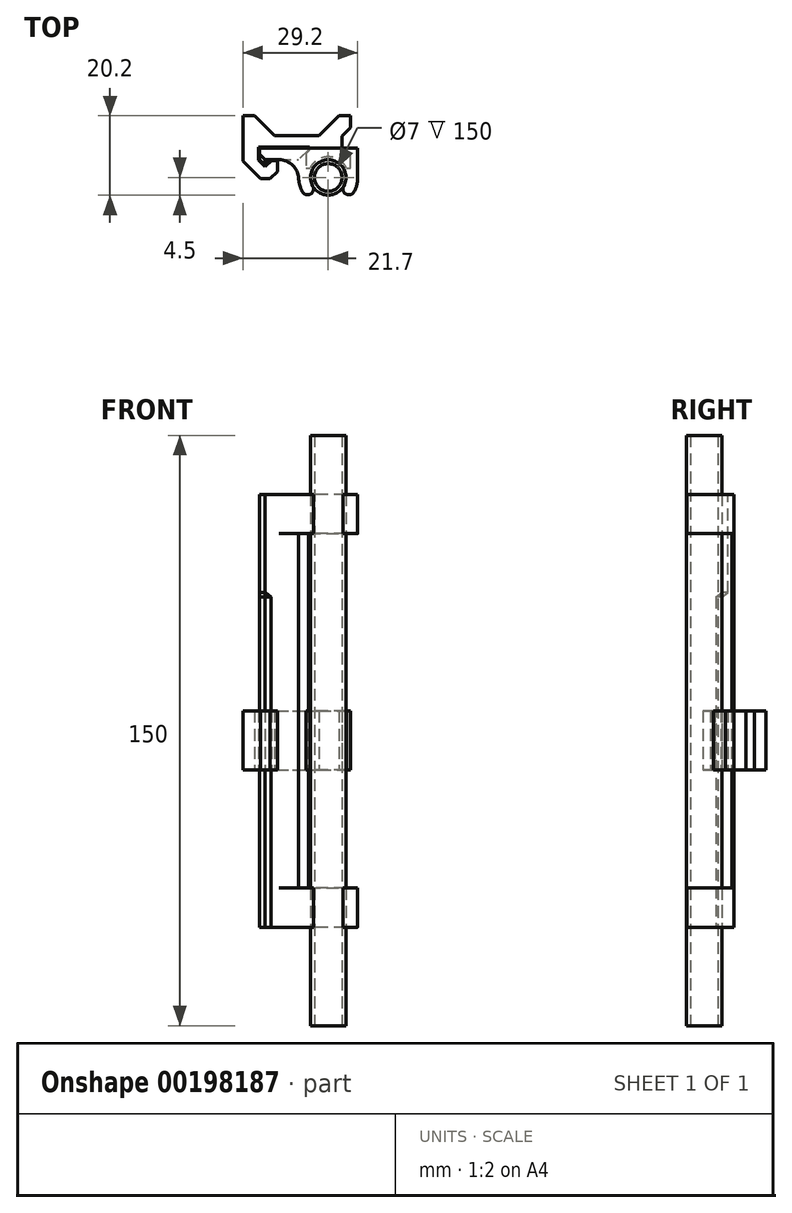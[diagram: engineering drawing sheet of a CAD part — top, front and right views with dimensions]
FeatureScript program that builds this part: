
annotation { "Feature Type Name" : "Feature", "Feature Type Description" : "" }
export const myFeature = defineFeature(function(context is Context, id is Id, definition is map)
    precondition{}
    {
        {
            var Q0;
            Q0=qCreatedBy(makeId("Top.planeOp"),FACE);
            var sketch = newSketch(context, id + "F0", { "sketchPlane" : qUnion([Q0])});
            skArc(sketch, "E0", {"start": v(-6.56, -3.63) * mm, "mid": v(-4.52, -4.22) * mm, "end": v(-3.94, -2.18) * mm});
            skArc(sketch, "E1.MirrorCS", {"start": v(6.56, -3.63) * mm, "mid": v(4.52, -4.22) * mm, "end": v(3.94, -2.18) * mm});
            skArc(sketch, "E2", {"start": v(-3.94, -2.18) * mm, "mid": v(0, -4.5) * mm, "end": v(3.94, -2.18) * mm, "construction": true});
            skArc(sketch, "E3", {"start": v(3.94, -2.18) * mm, "mid": v(0, 4.5) * mm, "end": v(-3.94, -2.18) * mm});
            skArc(sketch, "E4", {"start": v(6.56, -3.63) * mm, "mid": v(7.26, -1.87) * mm, "end": v(7.5, 0) * mm});
            skArc(sketch, "E5", {"start": v(-6.56, -3.63) * mm, "mid": v(0, -7.5) * mm, "end": v(6.56, -3.63) * mm, "construction": true});
            skLineSegment(sketch, "E6.right", {"start": v(-17.5, 4.5) * mm, "end": v(-17.5, 7.5) * mm});
            skArc(sketch, "E7", {"start": v(-7.5, 0) * mm, "mid": v(-7.26, -1.87) * mm, "end": v(-6.56, -3.63) * mm});
            skLineSegment(sketch, "E8", {"start": v(-7.5, 4.5) * mm, "end": v(-17.5, 4.5) * mm});
            skArc(sketch, "E9", {"start": v(7.5, 0) * mm, "mid": v(0, 7.5) * mm, "end": v(-7.5, 0) * mm, "construction": true});
            skLineSegment(sketch, "E10", {"start": v(7.5, 0) * mm, "end": v(7.5, 7.5) * mm});
            skPoint(sketch, "E10.endSnap0", {"position": v(0, 7.5) * mm});
            skLineSegment(sketch, "E11", {"start": v(-17.5, 7.5) * mm, "end": v(7.5, 7.5) * mm});
            skLineSegment(sketch, "E12", {"start": v(-7.5, 0) * mm, "end": v(-7.5, 4.5) * mm});
            skLineSegment(sketch, "E13", {"start": v(-4.5, 0) * mm, "end": v(-4.5, 7.5) * mm, "construction": true});
            skLineSegment(sketch, "E14", {"start": v(-7.5, 4.5) * mm, "end": v(-5, 7) * mm});
            skLineSegment(sketch, "E15", {"start": v(-5, 7) * mm, "end": v(-5, 7.5) * mm});
            skLineSegment(sketch, "E16", {"start": v(-5, 7) * mm, "end": v(-4.5, 7.5) * mm, "construction": true});
            skLineSegment(sketch, "E17", {"start": v(-17.5, 4.5) * mm, "end": v(-16, 3) * mm});
            skLineSegment(sketch, "E18", {"start": v(-16, 3) * mm, "end": v(-14.5, 4.5) * mm});
            skSolve(sketch);
        }
        {
            var Q0;
            Q0=qCreatedBy(makeId("Top.planeOp"),FACE);
            var sketch = newSketch(context, id + "F1", { "sketchPlane" : qUnion([Q0])});
            skCircle(sketch, "E19", {"center": v(0, 0) * mm, "radius": 4.5 * mm});
            skCircle(sketch, "E20", {"center": v(0, 0) * mm, "radius": 3.5 * mm});
            skSolve(sketch);
        }
        {
            var Q0;
            Q0=qCreatedBy(makeId("Top.planeOp"),FACE);
            var sketch = newSketch(context, id + "F2", { "sketchPlane" : qUnion([Q0])});
            skLineSegment(sketch, "E21.0", {"start": v(-17.5, 4.5) * mm, "end": v(-17.5, 7.5) * mm, "construction": true});
            skLineSegment(sketch, "E22.0", {"start": v(-17.5, 4.5) * mm, "end": v(-16, 3) * mm, "construction": true});
            skLineSegment(sketch, "E23.0", {"start": v(-16, 3) * mm, "end": v(-14.5, 4.5) * mm, "construction": true});
            skLineSegment(sketch, "E24.0", {"start": v(-7.5, 4.5) * mm, "end": v(-14.5, 4.5) * mm, "construction": true});
            skLineSegment(sketch, "E25.0", {"start": v(-7.5, 4.5) * mm, "end": v(-5, 7) * mm, "construction": true});
            skLineSegment(sketch, "E26.0", {"start": v(-5, 7) * mm, "end": v(-5, 7.5) * mm, "construction": true});
            skLineSegment(sketch, "E27.0", {"start": v(-17.5, 7.5) * mm, "end": v(-5, 7.5) * mm, "construction": true});
            skPoint(sketch, "E28.orphan", {"position": v(-17.5, 4.5) * mm});
            skLineSegment(sketch, "E29.0", {"start": v(-17.7, 4.42) * mm, "end": v(-17.7, 7.7) * mm});
            skLineSegment(sketch, "E29.1", {"start": v(-17.7, 4.42) * mm, "end": v(-16, 2.72) * mm});
            skLineSegment(sketch, "E29.2", {"start": v(-4.8, 6.92) * mm, "end": v(-4.8, 7.7) * mm});
            skLineSegment(sketch, "E29.3", {"start": v(-5.68, 6.04) * mm, "end": v(-4.8, 6.92) * mm});
            skLineSegment(sketch, "E29.4", {"start": v(-7.42, 4.3) * mm, "end": v(-7.5, 4.3) * mm});
            skLineSegment(sketch, "E29.5", {"start": v(-17.7, 7.7) * mm, "end": v(-4.8, 7.7) * mm});
            skLineSegment(sketch, "E29.6", {"start": v(-16, 2.72) * mm, "end": v(-14.42, 4.3) * mm});
            skLineSegment(sketch, "E30.0", {"start": v(-7.5, 0) * mm, "end": v(-7.5, 4.5) * mm, "construction": true});
            skArc(sketch, "E31", {"start": v(-7.5, -0.5) * mm, "mid": v(-8.96, 3.04) * mm, "end": v(-12.5, 4.5) * mm, "construction": true});
            skLineSegment(sketch, "E32", {"start": v(-12.92, 4.3) * mm, "end": v(-12.92, 1.56) * mm});
            skLineSegment(sketch, "E33", {"start": v(-12.92, 1.56) * mm, "end": v(-14.76, -0.28) * mm});
            skLineSegment(sketch, "E34", {"start": v(-17.24, -0.28) * mm, "end": v(-21.7, 4.17) * mm});
            skLineSegment(sketch, "E35", {"start": v(-21.7, 4.17) * mm, "end": v(-21.7, 15.7) * mm});
            skLineSegment(sketch, "E36", {"start": v(-21.7, 15.7) * mm, "end": v(-18.7, 15.7) * mm});
            skLineSegment(sketch, "E37", {"start": v(-17.24, -0.28) * mm, "end": v(-14.76, -0.28) * mm});
            skPoint(sketch, "E38.orphan", {"position": v(-16, -1.53) * mm});
            skCircle(sketch, "E39.0", {"center": v(0, 0) * mm, "radius": 4.5 * mm, "construction": true});
            skLineSegment(sketch, "E40", {"start": v(-5.68, 6.04) * mm, "end": v(-5.68, 2.38) * mm});
            skArc(sketch, "E41", {"start": v(4.68, 2.38) * mm, "mid": v(0, 5.25) * mm, "end": v(-4.68, 2.38) * mm});
            skLineSegment(sketch, "E42", {"start": v(-5.68, 2.38) * mm, "end": v(-4.68, 2.38) * mm});
            skLineSegment(sketch, "E43", {"start": v(4.68, 2.38) * mm, "end": v(5.68, 2.38) * mm});
            skLineSegment(sketch, "E44", {"start": v(5.68, 2.38) * mm, "end": v(5.68, 5.38) * mm});
            skLineSegment(sketch, "E45.trimOffspring", {"start": v(-12.92, 4.3) * mm, "end": v(-14.42, 4.3) * mm});
            skLineSegment(sketch, "E46", {"start": v(-18.7, 15.7) * mm, "end": v(-13.7, 10.7) * mm});
            skLineSegment(sketch, "E47", {"start": v(-13.7, 10.7) * mm, "end": v(-2.32, 10.7) * mm});
            skLineSegment(sketch, "E48", {"start": v(-2.32, 10.7) * mm, "end": v(2.68, 15.7) * mm});
            skLineSegment(sketch, "E49.trimOffspring", {"start": v(2.68, 15.7) * mm, "end": v(5.68, 15.7) * mm});
            skLineSegment(sketch, "E50", {"start": v(5.68, 12.7) * mm, "end": v(3.52, 10.54) * mm});
            skLineSegment(sketch, "E51", {"start": v(3.52, 10.54) * mm, "end": v(3.52, 7.54) * mm});
            skLineSegment(sketch, "E52", {"start": v(3.52, 7.54) * mm, "end": v(5.68, 5.38) * mm});
            skLineSegment(sketch, "E53.trimOffspring", {"start": v(5.68, 12.7) * mm, "end": v(5.68, 15.7) * mm});
            skSolve(sketch);
        }
        {
            var Q0;
            {var subQ0=sQuery(id+"F0.wireOp",EDGE,"E6.right");Q0=makeQuery(id+"F0.imprint","IMPRINT",FACE,{"disambiguationData":[TD([[makeQuery(id+"F0.imprint","IMPRINT",EDGE,{"derivedFrom":subQ0}),-1.0]])]});}
            var Q1;
            Q1=makeQuery(id+"F0.imprint","IMPRINT",FACE,{"disambiguationData":[TD([[makeQuery(id+"F0.imprint","IMPRINT",EDGE,{"derivedFrom":sQuery(id+"F0.wireOp",EDGE,"E0")}),1.0]])]});
            var Q2;
            {var subQ0=sQuery(id+"F0.wireOp",EDGE,"E12");Q2=makeQuery(id+"F0.imprint","IMPRINT",FACE,{"disambiguationData":[TD([[makeQuery(id+"F0.imprint","IMPRINT",EDGE,{"derivedFrom":subQ0}),1.0]])]});}
            extrude(context, id + "F3", {"entities" : qUnion([Q0, Q1, Q2]), "depth" : 10 * mm});
        }
        {
            var Q0;
            Q0=makeQuery(id+"F3.opExtrude","CAP_FACE",FACE,{"disambiguationData":[OSD([sQuery(id+"F0.wireOp",EDGE,"E0"),sQuery(id+"F0.wireOp",EDGE,"E1.MirrorCS"),sQuery(id+"F0.wireOp",EDGE,"E3"),sQuery(id+"F0.wireOp",EDGE,"E4"),sQuery(id+"F0.wireOp",EDGE,"E6.right"),sQuery(id+"F0.wireOp",EDGE,"E7"),sQuery(id+"F0.wireOp",EDGE,"E8"),sQuery(id+"F0.wireOp",EDGE,"E10"),sQuery(id+"F0.wireOp",EDGE,"E11"),sQuery(id+"F0.wireOp",EDGE,"I9ya9IAf-afc4-xhVU-ryTu-VtxpZfvQhWm0")])],"isStart":true});
            extrude(context, id + "F4", {"entities" : qUnion([Q0]), "oppositeDirection" : true, "depth" : 110 * mm, "hasSecondDirection" : true, "secondDirectionOppositeDirection" : true, "secondDirectionDepth" : 100 * mm});
        }
        {
            var Q0;
            {var subQ0=sQuery(id+"F0.wireOp",EDGE,"E6.right");Q0=makeQuery(id+"F0.imprint","IMPRINT",FACE,{"disambiguationData":[TD([[makeQuery(id+"F0.imprint","IMPRINT",EDGE,{"derivedFrom":subQ0}),-1.0]])]});}
            var Q1;
            {var subQ0=sQuery(id+"F0.wireOp",EDGE,"unjN040T-zaWb-rErZ-I2JQ-GeDMov3pJUcJ");Q1=makeQuery(id+"F0.imprint","IMPRINT",FACE,{"disambiguationData":[TD([[makeQuery(id+"F0.imprint","IMPRINT",EDGE,{"derivedFrom":subQ0}),1.0]])]});}
            var Q2;
            Q2=makeQuery(id+"F4.opExtrude","CAP_FACE",FACE,{"disambiguationData":[OSD([sQuery(id+"F0.wireOp",EDGE,"E0"),sQuery(id+"F0.wireOp",EDGE,"E1.MirrorCS"),sQuery(id+"F0.wireOp",EDGE,"E3"),sQuery(id+"F0.wireOp",EDGE,"E4"),sQuery(id+"F0.wireOp",EDGE,"E6.right"),sQuery(id+"F0.wireOp",EDGE,"E7"),sQuery(id+"F0.wireOp",EDGE,"E8"),sQuery(id+"F0.wireOp",EDGE,"E10"),sQuery(id+"F0.wireOp",EDGE,"E11"),sQuery(id+"F0.wireOp",EDGE,"E12")])],"isStart":false});
            extrude(context, id + "F5", {"entities" : qUnion([Q0, Q1]), "operationType" : NewBodyOperationType.ADD, "endBound" : BoundingType.UP_TO_SURFACE, "endBoundEntityFace" : qUnion([Q2]), "depth" : 25 * mm});
        }
        {
            var Q0;
            {var subQ0=sQuery(id+"F0.wireOp",EDGE,"E17");Q0=makeQuery(id+"F0.imprint","IMPRINT",FACE,{"disambiguationData":[TD([[makeQuery(id+"F0.imprint","IMPRINT",EDGE,{"derivedFrom":subQ0}),1.0]])]});}
            extrude(context, id + "F6", {"entities" : qUnion([Q0]), "operationType" : NewBodyOperationType.ADD, "depth" : 85 * mm});
        }
        {
            var Q0;
            Q0=makeQuery(id+"F3.opExtrude","SWEPT_EDGE",EDGE,{"disambiguationData":[OSD([sQuery(id+"F0.wireOp",EDGE,"E8"),sQuery(id+"F0.wireOp",EDGE,"E12"),sQuery(id+"F0.wireOp",EDGE,"E14")])]});
            var Q1;
            Q1=makeQuery(id+"F4.opExtrude","SWEPT_EDGE",EDGE,{"disambiguationData":[OSD([sQuery(id+"F0.wireOp",EDGE,"E8"),sQuery(id+"F0.wireOp",EDGE,"E12"),sQuery(id+"F0.wireOp",EDGE,"E14")])]});
            fillet(context, id + "F7", {"entities" : qUnion([Q0, Q1]), "radius" : 5 * mm, "tangentPropagation" : true, "allowEdgeOverflow" : false});
        }
        {
            var Q0;
            Q0=makeQuery(id+"F1.imprint","IMPRINT",FACE,{"disambiguationData":[TD([[makeQuery(id+"F1.imprint","IMPRINT",EDGE,{"derivedFrom":sQuery(id+"F1.wireOp",EDGE,"E19")}),1.0]])]});
            extrude(context, id + "F8", {"entities" : qUnion([Q0]), "depth" : 125 * mm, "hasSecondDirection" : true, "secondDirectionOppositeDirection" : true, "secondDirectionDepth" : 25 * mm});
        }
        {
            var Q0;
            Q0=makeQuery(id+"F2.imprint","IMPRINT",FACE,{"disambiguationData":[TD([[makeQuery(id+"F2.imprint","IMPRINT",EDGE,{"derivedFrom":sQuery(id+"F2.wireOp",EDGE,"E29.0")}),1.0]])]});
            extrude(context, id + "F9", {"entities" : qUnion([Q0]), "depth" : 55 * mm, "hasSecondDirection" : true, "secondDirectionOppositeDirection" : false, "secondDirectionDepth" : 40 * mm});
        }
        {
            var Q0;
            {var subQ0=sQuery(id+"F0.wireOp",EDGE,"E17");var subQ1=sQuery(id+"F0.wireOp",EDGE,"E8");var subQ2=sQuery(id+"F0.wireOp",EDGE,"E6.right");Q0=makeQuery(id+"F6.boolean.opBoolean","SPLIT",EDGE,{"derivedFrom":makeQuery(id+"F5.boolean.opBoolean","MERGE",EDGE,{"derivedFrom":[makeQuery(id+"F3.opExtrude","SWEPT_EDGE",EDGE,{"disambiguationData":[OSD([subQ2,subQ1,subQ0])]}),makeQuery(id+"F4.opExtrude","SWEPT_EDGE",EDGE,{"disambiguationData":[OSD([subQ2,subQ1,subQ0])]}),makeQuery(id+"F5.opExtrude","SWEPT_EDGE",EDGE,{"disambiguationData":[OSD([subQ2,subQ1,subQ0])]})]})});}
            chamfer(context, id + "F10", {"entities" : qUnion([Q0]), "width" : 1.5 * mm, "tangentPropagation" : true});
        }
        {
            var Q0;
            Q0=makeQuery(id+"F6.opExtrude","CAP_EDGE",EDGE,{"disambiguationData":[OSD([sQuery(id+"F0.wireOp",EDGE,"E17")])],"isStart":false});
            var Q1;
            Q1=makeQuery(id+"F6.opExtrude","CAP_EDGE",EDGE,{"disambiguationData":[OSD([sQuery(id+"F0.wireOp",EDGE,"E18")])],"isStart":false});
            chamfer(context, id + "F11", {"entities" : qUnion([Q0, Q1]), "width" : 1.05 * mm, "tangentPropagation" : true});
        }
    });
